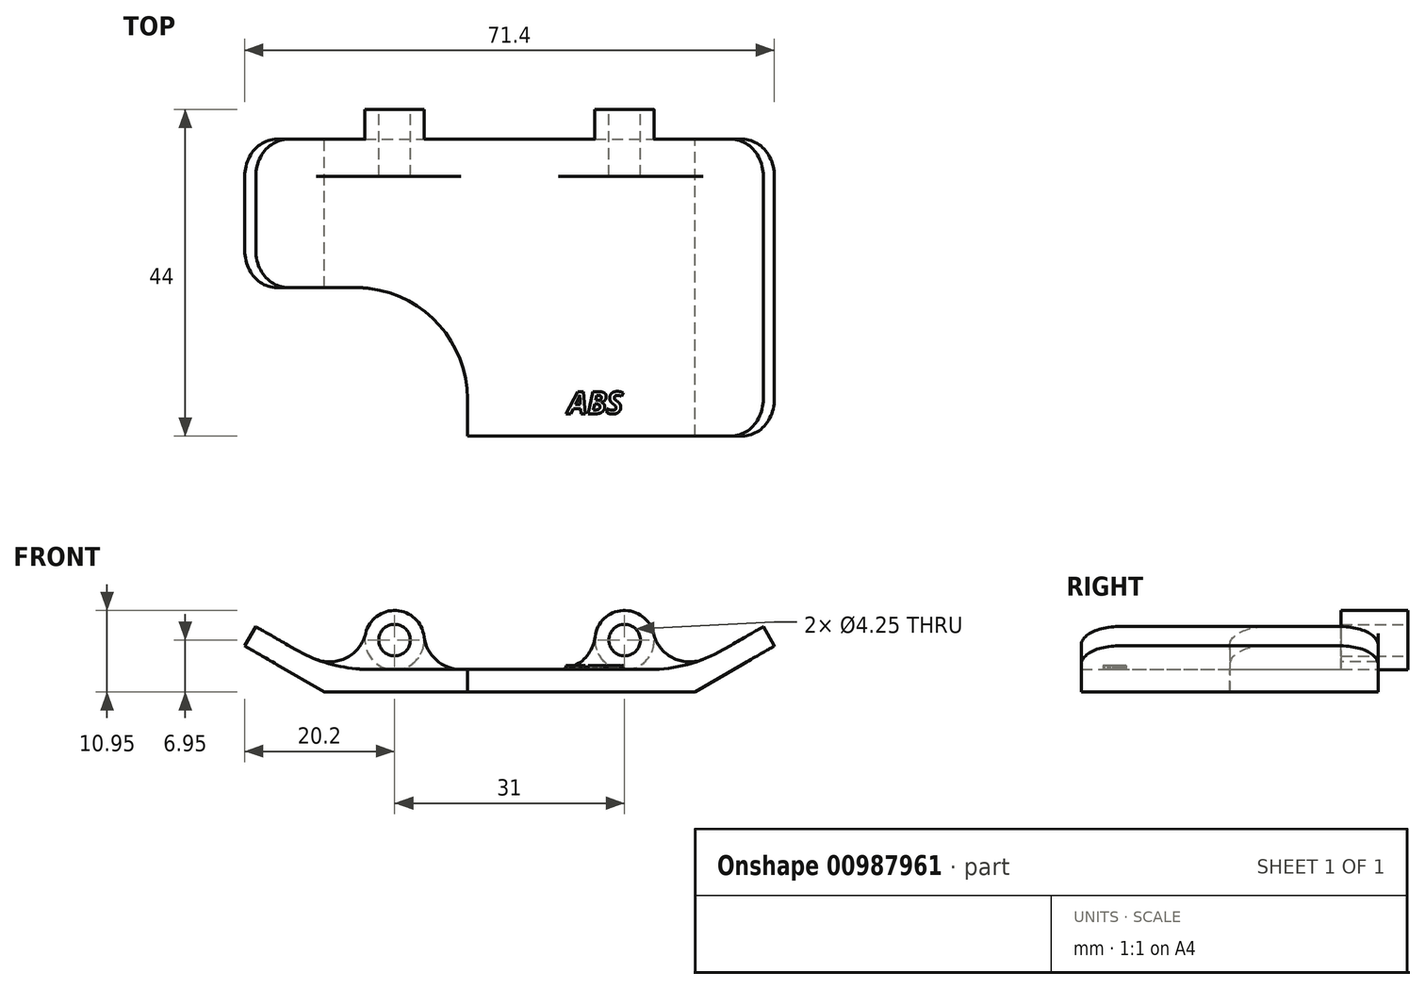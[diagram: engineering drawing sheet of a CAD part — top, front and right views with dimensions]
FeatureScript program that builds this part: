
annotation { "Feature Type Name" : "Feature", "Feature Type Description" : "" }
export const myFeature = defineFeature(function(context is Context, id is Id, definition is map)
    precondition{}
    {
        {
            var Q0;
            Q0=qCreatedBy(makeId("Front.planeOp"),FACE);
            var sketch = newSketch(context, id + "F0", { "sketchPlane" : qUnion([Q0])});
            skCircle(sketch, "E0", {"center": v(15.5, 0) * mm, "radius": 4 * mm});
            skCircle(sketch, "E1", {"center": v(-15.5, 0) * mm, "radius": 4 * mm});
            skLineSegment(sketch, "E2", {"start": v(-15.5, 0) * mm, "end": v(0, 0) * mm, "construction": true});
            skLineSegment(sketch, "E3", {"start": v(0, 0) * mm, "end": v(15.5, 0) * mm, "construction": true});
            skCircle(sketch, "E4", {"center": v(-15.5, 0) * mm, "radius": 2.12 * mm});
            skCircle(sketch, "E5", {"center": v(15.5, 0) * mm, "radius": 2.12 * mm});
            skSolve(sketch);
        }
        {
            var Q0;
            Q0 = qSketchRegion(id + "F0", true);
            extrude(context, id + "F1", {"entities" : qUnion([Q0]), "depth" : 9 * mm, "offsetDistance" : 25 * mm});
        }
        {
            var Q0;
            Q0=makeQuery(id+"F1.opExtrude","CAP_FACE",FACE,{"disambiguationData":[OSD([sQuery(id+"F0.wireOp",EDGE,"E0"),sQuery(id+"F0.wireOp",EDGE,"E5")])],"isStart":false});
            cPlane(context, id + "F2", {"entities" : qUnion([Q0]), "cplaneType" : CPlaneType.OFFSET, "offset" : 5 * mm, "oppositeDirection" : true, "width" : 150 * mm, "height" : 150 * mm});
        }
        {
            var Q0;
            Q0=qCreatedBy(id+"F2.planeOp",FACE);
            var sketch = newSketch(context, id + "F3", { "sketchPlane" : qUnion([Q0])});
            skLineSegment(sketch, "E6.bottom", {"start": v(-24.2, -3.95) * mm, "end": v(24.2, -3.95) * mm});
            skLineSegment(sketch, "E6.top", {"start": v(-25, -6.95) * mm, "end": v(25, -6.95) * mm});
            skLineSegment(sketch, "E7", {"start": v(0, 0) * mm, "end": v(0, 21.45) * mm, "construction": true});
            skLineSegment(sketch, "E8", {"start": v(24.2, -3.95) * mm, "end": v(34.2, 1.82) * mm});
            skLineSegment(sketch, "E9", {"start": v(34.2, 1.82) * mm, "end": v(35.7, -0.77) * mm});
            skLineSegment(sketch, "E10", {"start": v(35.7, -0.77) * mm, "end": v(25, -6.95) * mm});
            skLineSegment(sketch, "E11", {"start": v(-24.2, -3.95) * mm, "end": v(-34.2, 1.82) * mm});
            skLineSegment(sketch, "E12", {"start": v(-34.2, 1.82) * mm, "end": v(-35.7, -0.77) * mm});
            skLineSegment(sketch, "E13", {"start": v(-35.7, -0.77) * mm, "end": v(-25, -6.95) * mm});
            skLineSegment(sketch, "E14", {"start": v(-24.2, -3.95) * mm, "end": v(-25, -6.95) * mm, "construction": true});
            skLineSegment(sketch, "E15", {"start": v(24.2, -3.95) * mm, "end": v(25, -6.95) * mm, "construction": true});
            skSolve(sketch);
        }
        {
            var Q0;
            Q0 = qSketchRegion(id + "F3", true);
            extrude(context, id + "F4", {"entities" : qUnion([Q0]), "operationType" : NewBodyOperationType.ADD, "depth" : 40 * mm, "offsetDistance" : 25 * mm});
        }
        {
            var Q0;
            Q0=makeQuery(id+"F4.opExtrude","SWEPT_EDGE",EDGE,{"disambiguationData":[OSD([sQuery(id+"F3.wireOp",EDGE,"E6.bottom"),sQuery(id+"F3.wireOp",EDGE,"E8")])]});
            var Q1;
            Q1=makeQuery(id+"F4.opExtrude","SWEPT_EDGE",EDGE,{"disambiguationData":[OSD([sQuery(id+"F3.wireOp",EDGE,"E6.bottom"),sQuery(id+"F3.wireOp",EDGE,"E11")])]});
            fillet(context, id + "F5", {"entities" : qUnion([Q0, Q1]), "radius" : 20 * mm, "tangentPropagation" : true, "allowEdgeOverflow" : false});
        }
        {
            var Q0;
            Q0=makeQuery(id+"F4.boolean.opBoolean","INTERSECT",EDGE,{"disambiguationData":[OD(0.0)],"derivedFrom":[makeQuery(id+"F1.opExtrude","SWEPT_FACE",FACE,{"disambiguationData":[OSD([sQuery(id+"F0.wireOp",EDGE,"E0")])]}),makeQuery(id+"F4.opExtrude","SWEPT_FACE",FACE,{"disambiguationData":[OSD([sQuery(id+"F3.wireOp",EDGE,"E6.bottom")])]})]});
            var Q1;
            Q1=makeQuery(id+"F4.boolean.opBoolean","INTERSECT",EDGE,{"disambiguationData":[OD(1.0)],"derivedFrom":[makeQuery(id+"F1.opExtrude","SWEPT_FACE",FACE,{"disambiguationData":[OSD([sQuery(id+"F0.wireOp",EDGE,"E0")])]}),makeQuery(id+"F4.opExtrude","SWEPT_FACE",FACE,{"disambiguationData":[OSD([sQuery(id+"F3.wireOp",EDGE,"E6.bottom")])]})]});
            var Q2;
            Q2=makeQuery(id+"F4.boolean.opBoolean","INTERSECT",EDGE,{"disambiguationData":[OD(0.0)],"derivedFrom":[makeQuery(id+"F1.opExtrude","SWEPT_FACE",FACE,{"disambiguationData":[OSD([sQuery(id+"F0.wireOp",EDGE,"E1")])]}),makeQuery(id+"F4.opExtrude","SWEPT_FACE",FACE,{"disambiguationData":[OSD([sQuery(id+"F3.wireOp",EDGE,"E6.bottom")])]})]});
            var Q3;
            Q3=makeQuery(id+"F4.boolean.opBoolean","INTERSECT",EDGE,{"disambiguationData":[OD(1.0)],"derivedFrom":[makeQuery(id+"F1.opExtrude","SWEPT_FACE",FACE,{"disambiguationData":[OSD([sQuery(id+"F0.wireOp",EDGE,"E1")])]}),makeQuery(id+"F4.opExtrude","SWEPT_FACE",FACE,{"disambiguationData":[OSD([sQuery(id+"F3.wireOp",EDGE,"E6.bottom")])]})]});
            fillet(context, id + "F6", {"entities" : qUnion([Q0, Q1, Q2, Q3]), "radius" : 5 * mm, "allowEdgeOverflow" : false});
        }
        {
            var Q0;
            Q0=makeQuery(id+"F4.opExtrude","SWEPT_FACE",FACE,{"disambiguationData":[OSD([sQuery(id+"F3.wireOp",EDGE,"E6.bottom")])]});
            var sketch = newSketch(context, id + "F7", { "sketchPlane" : qUnion([Q0])});
            skLineSegment(sketch, "E16.bottom", {"start": v(-35.7, -44) * mm, "end": v(-5.7, -44) * mm});
            skLineSegment(sketch, "E16.top", {"start": v(-35.7, -24) * mm, "end": v(-5.7, -24) * mm});
            skLineSegment(sketch, "E16.left", {"start": v(-35.7, -44) * mm, "end": v(-35.7, -24) * mm});
            skLineSegment(sketch, "E16.right", {"start": v(-5.7, -44) * mm, "end": v(-5.7, -24) * mm});
            skSolve(sketch);
        }
        {
            var Q0;
            Q0 = qSketchRegion(id + "F7", true);
            extrude(context, id + "F8", {"entities" : qUnion([Q0]), "operationType" : NewBodyOperationType.REMOVE, "endBound" : BoundingType.THROUGH_ALL, "oppositeDirection" : true, "depth" : 25 * mm, "offsetDistance" : 25 * mm, "hasSecondDirection" : true, "secondDirectionBound" : SecondDirectionBoundingType.THROUGH_ALL, "secondDirectionOppositeDirection" : false, "secondDirectionDepth" : 25 * mm});
        }
        {
            var Q0;
            Q0=makeQuery(id+"F8.boolean.opBoolean","COPY",EDGE,{"derivedFrom":makeQuery(id+"F8.opExtrude","SWEPT_EDGE",EDGE,{"disambiguationData":[OSD([sQuery(id+"F7.wireOp",EDGE,"E16.top"),sQuery(id+"F7.wireOp",EDGE,"E16.right")])]})});
            fillet(context, id + "F9", {"entities" : qUnion([Q0]), "radius" : 15 * mm, "tangentPropagation" : true, "allowEdgeOverflow" : false});
        }
        {
            var Q0;
            Q0=makeQuery(id+"F4.opExtrude","CAP_EDGE",EDGE,{"disambiguationData":[OSD([sQuery(id+"F3.wireOp",EDGE,"E12")])],"isStart":true});
            var Q1;
            Q1=makeQuery(id+"F8.boolean.opBoolean","COPY",EDGE,{"derivedFrom":makeQuery(id+"F8.opExtrude","SWEPT_EDGE",EDGE,{"disambiguationData":[OSD([sQuery(id+"F3.wireOp",EDGE,"E6.bottom"),sQuery(id+"F7.wireOp",EDGE,"E16.bottom"),sQuery(id+"F7.wireOp",EDGE,"E16.right")])]})});
            var Q2;
            Q2=makeQuery(id+"F4.opExtrude","CAP_EDGE",EDGE,{"disambiguationData":[OSD([sQuery(id+"F3.wireOp",EDGE,"E9")])],"isStart":true});
            var Q3;
            Q3=makeQuery(id+"F8.boolean.opBoolean","INTERSECT",EDGE,{"derivedFrom":[makeQuery(id+"F4.opExtrude","SWEPT_FACE",FACE,{"disambiguationData":[OSD([sQuery(id+"F3.wireOp",EDGE,"E12")])]}),makeQuery(id+"F8.opExtrude","SWEPT_FACE",FACE,{"disambiguationData":[OSD([sQuery(id+"F7.wireOp",EDGE,"E16.top")])]})]});
            var Q4;
            Q4=makeQuery(id+"F4.opExtrude","CAP_EDGE",EDGE,{"disambiguationData":[OSD([sQuery(id+"F3.wireOp",EDGE,"E9")])],"isStart":false});
            fillet(context, id + "F10", {"entities" : qUnion([Q0, Q1, Q2, Q3, Q4]), "radius" : 5 * mm, "tangentPropagation" : true, "allowEdgeOverflow" : false});
        }
        {
            var Q0;
            Q0=makeQuery(id+"F4.opExtrude","SWEPT_FACE",FACE,{"disambiguationData":[OSD([sQuery(id+"F3.wireOp",EDGE,"E6.bottom")])]});
            var sketch = newSketch(context, id + "F11", { "sketchPlane" : qUnion([Q0])});
            skText(sketch, "E17", { "text": "ABS", "fontName": "OpenSans-BoldItalic.ttf"});
            const initialGuessF11  = {"E17": [0.00786, -0.041, 1, 0, 0.003]};
            skSetInitialGuess(sketch, initialGuessF11);
            skSolve(sketch);
        }
        {
            var Q0;
            Q0 = qSketchRegion(id + "F11", true);
            extrude(context, id + "F12", {"entities" : qUnion([Q0]), "operationType" : NewBodyOperationType.ADD, "depth" : 0.5 * mm, "offsetDistance" : 25 * mm});
        }
    });
